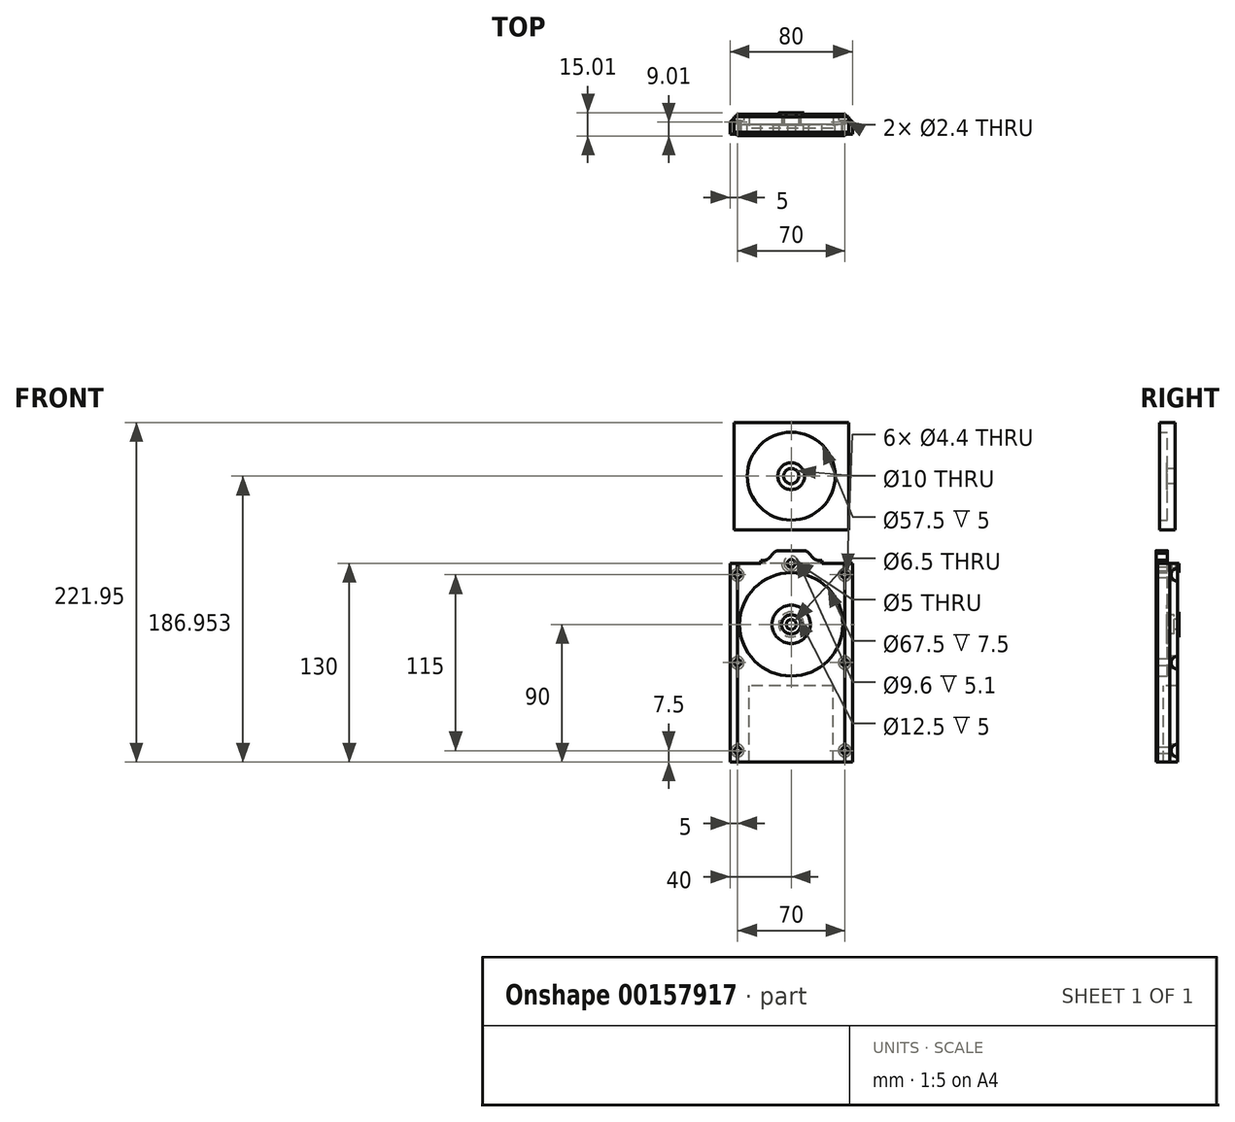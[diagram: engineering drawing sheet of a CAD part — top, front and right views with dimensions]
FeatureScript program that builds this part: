
annotation { "Feature Type Name" : "Feature", "Feature Type Description" : "" }
export const myFeature = defineFeature(function(context is Context, id is Id, definition is map)
    precondition{}
    {
        {
            var Q0;
            Q0=qCreatedBy(makeId("Front.planeOp"),FACE);
            var sketch = newSketch(context, id + "F0", { "sketchPlane" : qUnion([Q0])});
            skLineSegment(sketch, "E0.0", {"start": v(40, -23.23) * mm, "end": v(40, 0.77) * mm});
            skLineSegment(sketch, "E1.0", {"start": v(-40, -23.23) * mm, "end": v(-40, 0.77) * mm});
            skLineSegment(sketch, "E2.bottom", {"start": v(40, 40) * mm, "end": v(19.39, 40) * mm});
            skLineSegment(sketch, "E2.top", {"start": v(40, -40) * mm, "end": v(-40, -40) * mm});
            skLineSegment(sketch, "E2.left", {"start": v(40, 40) * mm, "end": v(40, -40) * mm});
            skLineSegment(sketch, "E2.right", {"start": v(-40, 40) * mm, "end": v(-40, -40) * mm});
            skCircle(sketch, "E3.0", {"center": v(0, 0) * mm, "radius": 3.25 * mm});
            skLineSegment(sketch, "E4.0", {"start": v(7.32, 48.27) * mm, "end": v(-8.54, 48.27) * mm});
            skArc(sketch, "E5.0", {"start": v(-8.54, 48.27) * mm, "mid": v(-10.45, 47.89) * mm, "end": v(-12.08, 46.8) * mm});
            skLineSegment(sketch, "E6.0", {"start": v(-12.08, 46.8) * mm, "end": v(-15.65, 43.23) * mm});
            skArc(sketch, "E7.0", {"start": v(-19.18, 41.77) * mm, "mid": v(-17.27, 42.15) * mm, "end": v(-15.65, 43.23) * mm});
            skLineSegment(sketch, "E8.0", {"start": v(-20.61, 41.77) * mm, "end": v(-19.18, 41.77) * mm});
            skLineSegment(sketch, "E9.0", {"start": v(-20.61, 40) * mm, "end": v(-20.61, 41.77) * mm});
            skArc(sketch, "E10.0", {"start": v(7.32, 48.27) * mm, "mid": v(9.23, 47.89) * mm, "end": v(10.85, 46.8) * mm});
            skLineSegment(sketch, "E11.0", {"start": v(10.85, 46.8) * mm, "end": v(14.42, 43.23) * mm});
            skArc(sketch, "E12.0", {"start": v(17.96, 41.77) * mm, "mid": v(16.05, 42.15) * mm, "end": v(14.42, 43.23) * mm});
            skLineSegment(sketch, "E13.0", {"start": v(19.39, 40) * mm, "end": v(19.39, 41.77) * mm});
            skLineSegment(sketch, "E14", {"start": v(17.96, 41.77) * mm, "end": v(19.39, 41.77) * mm});
            skLineSegment(sketch, "E15.trimOffspring", {"start": v(-20.61, 40) * mm, "end": v(-40, 40) * mm});
            skLineSegment(sketch, "E16", {"start": v(-20.61, 40) * mm, "end": v(19.39, 40) * mm});
            skSolve(sketch);
        }
        {
            var Q0;
            {var subQ4=sQuery(id+"F0.wireOp",EDGE,"E2.bottom");Q0=makeQuery(id+"F0.imprint","IMPRINT",FACE,{"disambiguationData":[TD([[makeQuery(id+"F0.imprint","IMPRINT",EDGE,{"derivedFrom":subQ4}),1.0]])]});}
            extrude(context, id + "F1", {"entities" : qUnion([Q0]), "oppositeDirection" : true, "depth" : 6.5 * mm});
        }
        {
            var Q0;
            Q0=qCreatedBy(makeId("Front.planeOp"),FACE);
            var sketch = newSketch(context, id + "F2", { "sketchPlane" : qUnion([Q0])});
            skCircle(sketch, "E17.0", {"center": v(0, 0) * mm, "radius": 6.3 * mm});
            skLineSegment(sketch, "E18", {"start": v(-40, -40) * mm, "end": v(40, -40) * mm});
            skCircle(sketch, "E19", {"center": v(0, 0) * mm, "radius": 33.75 * mm});
            skLineSegment(sketch, "E20", {"start": v(40, -40) * mm, "end": v(40, 40) * mm});
            skLineSegment(sketch, "E21.0", {"start": v(7.93, 48.27) * mm, "end": v(-7.93, 48.27) * mm});
            skLineSegment(sketch, "E22.0", {"start": v(11.66, 46.56) * mm, "end": v(14.5, 43.42) * mm});
            skLineSegment(sketch, "E23", {"start": v(-40, 40) * mm, "end": v(-40, -40) * mm});
            skLineSegment(sketch, "E24", {"start": v(-20, 40) * mm, "end": v(-40, 40) * mm});
            skLineSegment(sketch, "E25", {"start": v(19.2, 40) * mm, "end": v(40, 40) * mm});
            skLineSegment(sketch, "E26", {"start": v(20, 41.79) * mm, "end": v(20, 40) * mm});
            skLineSegment(sketch, "E27", {"start": v(20, 41.79) * mm, "end": v(18.2, 41.79) * mm});
            skArc(sketch, "E28", {"start": v(14.5, 43.42) * mm, "mid": v(16.18, 42.22) * mm, "end": v(18.2, 41.79) * mm});
            skArc(sketch, "E29", {"start": v(11.66, 46.56) * mm, "mid": v(10, 47.86) * mm, "end": v(7.93, 48.27) * mm});
            skArc(sketch, "E30.MirrorCS", {"start": v(-14.5, 43.42) * mm, "mid": v(-16.18, 42.22) * mm, "end": v(-18.2, 41.79) * mm});
            skLineSegment(sketch, "E31.MirrorCS", {"start": v(-20, 41.79) * mm, "end": v(-20, 40) * mm});
            skLineSegment(sketch, "E32.MirrorCS", {"start": v(-20, 41.79) * mm, "end": v(-18.2, 41.79) * mm});
            skLineSegment(sketch, "E33.MirrorCS", {"start": v(-11.66, 46.56) * mm, "end": v(-14.5, 43.42) * mm});
            skArc(sketch, "E34.MirrorCS", {"start": v(-11.66, 46.56) * mm, "mid": v(-10, 47.86) * mm, "end": v(-7.93, 48.27) * mm});
            skSolve(sketch);
        }
        {
            var Q0;
            Q0 = qSketchRegion(id + "F2", true);
            extrude(context, id + "F3", {"entities" : qUnion([Q0]), "operationType" : NewBodyOperationType.ADD, "depth" : 7.5 * mm});
        }
        {
            var Q0;
            {var subQ0=sQuery(id+"F0.wireOp",EDGE,"E3.0");Q0=makeQuery(id+"F3.boolean.opBoolean","SPLIT",FACE,{"disambiguationData":[TD([makeQuery(id+"F1.opExtrude","SWEPT_FACE",FACE,{"disambiguationData":[OSD([subQ0])]})])],"derivedFrom":makeQuery(id+"F1.opExtrude","CAP_FACE",FACE,{"disambiguationData":[OSD([sQuery(id+"F0.wireOp",EDGE,"E2.bottom"),sQuery(id+"F0.wireOp",EDGE,"E2.top"),sQuery(id+"F0.wireOp",EDGE,"E2.left"),sQuery(id+"F0.wireOp",EDGE,"E2.right"),subQ0,sQuery(id+"F0.wireOp",EDGE,"E15.trimOffspring"),sQuery(id+"F0.wireOp",EDGE,"E16")])],"isStart":true})});}
            var sketch = newSketch(context, id + "F4", { "sketchPlane" : qUnion([Q0])});
            skCircle(sketch, "E35.0", {"center": v(0, 0) * mm, "radius": 3.25 * mm});
            skCircle(sketch, "E36.0", {"center": v(0, 0) * mm, "radius": 12.5 * mm});
            skSolve(sketch);
        }
        {
            var Q0;
            Q0=makeQuery(id+"F4.imprint","IMPRINT",FACE,{"disambiguationData":[TD([[makeQuery(id+"F4.imprint","IMPRINT",EDGE,{"derivedFrom":sQuery(id+"F4.wireOp",EDGE,"E35.0")}),-1.0]])]});
            var Q1;
            Q1 = qConstructionFilter(qBodyType(qCreatedBy(id + "F4" ,EDGE), BodyType.WIRE), ConstructionObject.NO);
            extrude(context, id + "F5", {"entities" : qUnion([Q0]), "operationType" : NewBodyOperationType.ADD, "surfaceEntities" : qUnion([Q1]), "depth" : 0.5 * mm});
        }
        {
            var Q0;
            Q0=makeQuery(id+"F1.opExtrude","CAP_FACE",FACE,{"disambiguationData":[OSD([sQuery(id+"F0.wireOp",EDGE,"E2.bottom"),sQuery(id+"F0.wireOp",EDGE,"E2.top"),sQuery(id+"F0.wireOp",EDGE,"E2.left"),sQuery(id+"F0.wireOp",EDGE,"E2.right"),sQuery(id+"F0.wireOp",EDGE,"E3.0"),sQuery(id+"F0.wireOp",EDGE,"E15.trimOffspring"),sQuery(id+"F0.wireOp",EDGE,"E16")])],"isStart":false});
            var sketch = newSketch(context, id + "F6", { "sketchPlane" : qUnion([Q0])});
            skCircle(sketch, "E37.0", {"center": v(0, 0) * mm, "radius": 3.25 * mm});
            skCircle(sketch, "E38.0", {"center": v(0, 0) * mm, "radius": 8.25 * mm});
            skSolve(sketch);
        }
        {
            var Q0;
            Q0=makeQuery(id+"F6.imprint","IMPRINT",FACE,{"disambiguationData":[TD([[makeQuery(id+"F6.imprint","IMPRINT",EDGE,{"derivedFrom":sQuery(id+"F6.wireOp",EDGE,"E37.0")}),1.0]])]});
            var Q1;
            Q1 = qConstructionFilter(qBodyType(qCreatedBy(id + "F6" ,EDGE), BodyType.WIRE), ConstructionObject.NO);
            extrude(context, id + "F7", {"entities" : qUnion([Q0]), "operationType" : NewBodyOperationType.ADD, "surfaceEntities" : qUnion([Q1]), "depth" : 1 * mm});
        }
        {
            var Q0;
            Q0=makeQuery(id+"F3.opExtrude","SWEPT_FACE",FACE,{"disambiguationData":[OSD([sQuery(id+"F2.wireOp",EDGE,"E18")])]});
            var sketch = newSketch(context, id + "F8", { "sketchPlane" : qUnion([Q0])});
            skLineSegment(sketch, "E39.0", {"start": v(40, -6.5) * mm, "end": v(27.5, -6.5) * mm});
            skLineSegment(sketch, "E40.0", {"start": v(-35, 7.5) * mm, "end": v(35, 7.5) * mm});
            skLineSegment(sketch, "E41", {"start": v(-40, -6.5) * mm, "end": v(-40, 6.5) * mm});
            skPoint(sketch, "E42.orphan", {"position": v(-17.5, 7.5) * mm});
            skLineSegment(sketch, "E43", {"start": v(-35, 6.5) * mm, "end": v(-35, 7.5) * mm});
            skLineSegment(sketch, "E44", {"start": v(-35, 6.5) * mm, "end": v(-40, 6.5) * mm});
            skPoint(sketch, "E45.orphan", {"position": v(-40, 7.5) * mm});
            skLineSegment(sketch, "E46", {"start": v(40, 6.5) * mm, "end": v(35, 6.5) * mm});
            skLineSegment(sketch, "E47", {"start": v(35, 6.5) * mm, "end": v(35, 7.5) * mm});
            skLineSegment(sketch, "E48", {"start": v(27.5, -6.5) * mm, "end": v(27.5, 2.5) * mm});
            skLineSegment(sketch, "E49.MirrorCS", {"start": v(-27.5, -6.5) * mm, "end": v(-27.5, 2.5) * mm});
            skPoint(sketch, "E50.start.orphan", {"position": v(16.14, 2.5) * mm});
            skLineSegment(sketch, "E51.trimOffspring", {"start": v(-27.5, -6.5) * mm, "end": v(-40, -6.5) * mm});
            skLineSegment(sketch, "E52", {"start": v(27.5, 2.5) * mm, "end": v(-27.5, 2.5) * mm});
            skSolve(sketch);
        }
        {
            var Q0;
            {var subQ0=sQuery(id+"F8.wireOp",EDGE,"Noq1iZsC-02XE-U1bK-aTjG-XJcRZ1OyOBWc");var subQ1=sQuery(id+"F8.wireOp",EDGE,"E39.0");var subQ2=makeQuery(id+"F8.imprint","INTERSECT",VERTEX,{"derivedFrom":[subQ1,subQ0]});Q0=makeQuery(id+"F8.imprint","IMPRINT",FACE,{"disambiguationData":[TD([[makeQuery(id+"F8.imprint","IMPRINT",EDGE,{"disambiguationData":[TD([[subQ2,-1.0]])],"derivedFrom":subQ1}),-1.0]])]});}
            var Q1;
            {var subQ7=sQuery(id+"F8.wireOp",EDGE,"E41");Q1=makeQuery(id+"F8.imprint","IMPRINT",FACE,{"disambiguationData":[TD([[makeQuery(id+"F8.imprint","IMPRINT",EDGE,{"derivedFrom":subQ7}),-1.0]])]});}
            var Q2;
            Q2=makeQuery(id+"F8.imprint","IMPRINT",FACE,{"disambiguationData":[TD([[makeQuery(id+"F8.imprint","IMPRINT",EDGE,{"derivedFrom":sQuery(id+"F8.wireOp",EDGE,"E40.0")}),-1.0]])]});
            extrude(context, id + "F9", {"entities" : qUnion([Q0, Q1, Q2]), "operationType" : NewBodyOperationType.ADD, "depth" : 50 * mm});
        }
        {
            var Q0;
            {var subQ0=sQuery(id+"F2.wireOp",EDGE,"F8tKHy5X-4OjT-vRDI-xvfP-sps80f9JvOj5");var subQ1=sQuery(id+"F2.wireOp",EDGE,"E18");var subQ2=makeQuery(id+"F3.opExtrude","SWEPT_FACE",FACE,{"disambiguationData":[OSD([subQ1])]});Q0=makeQuery(id+"F9.boolean.opBoolean","SPLIT",FACE,{"disambiguationData":[TD([makeQuery(id+"F3.opExtrude","CAP_FACE",FACE,{"disambiguationData":[OSD([sQuery(id+"F2.wireOp",EDGE,"43ff70fc-8323-4c3b-be4f-e7dcd28128a2.0"),sQuery(id+"F2.wireOp",EDGE,"6a53bcd3-b350-4012-b1e6-f17d590e4d40.0"),sQuery(id+"F2.wireOp",EDGE,"d2d7cf8e-e79f-49f9-bd9e-9d3b9ff60ceb.0"),sQuery(id+"F2.wireOp",EDGE,"d467ac46-905b-445b-963e-ac5b84aad985.0"),sQuery(id+"F2.wireOp",EDGE,"bd112014-28de-4375-aa5b-1523fa892efe.0"),sQuery(id+"F2.wireOp",EDGE,"0f5d5f43-bfa9-40f1-814d-f970481e9f5a.0"),sQuery(id+"F2.wireOp",EDGE,"7188da67-afae-4a6f-96a4-23c76f9ca605.0"),sQuery(id+"F2.wireOp",EDGE,"be224130-12d7-4de9-89d5-a9a642df7f72.0"),sQuery(id+"F2.wireOp",EDGE,"49c1cc58-9d2c-462a-8fa2-00916c70b713.0"),sQuery(id+"F2.wireOp",EDGE,"3bd6d884-65c0-4bce-9f69-8ca00f18da7b.0"),sQuery(id+"F2.wireOp",EDGE,"5123f48f-925f-46dd-863a-fc0157268591"),sQuery(id+"F2.wireOp",EDGE,"62nOXX7M-Kpb4-EMSY-4AHT-RUUfIk4w2igv"),subQ1,subQ0,sQuery(id+"F2.wireOp",EDGE,"Frdd6jCd-H3OT-73R4-LAr2-6LJI8BfQxRTi"),sQuery(id+"F2.wireOp",EDGE,"cVu9BNWQ-aUoj-CZYY-OFb3-C1fxlzU4T7I8"),sQuery(id+"F2.wireOp",EDGE,"E19")])],"isStart":false}),subQ2,makeQuery(id+"F3.opExtrude","SWEPT_FACE",FACE,{"disambiguationData":[OSD([subQ0])]}),makeQuery(id+"F9.opExtrude","SWEPT_FACE",FACE,{"disambiguationData":[OSD([sQuery(id+"F8.wireOp",EDGE,"E40.0")])]}),makeQuery(id+"F9.opExtrude","SWEPT_FACE",FACE,{"disambiguationData":[OSD([sQuery(id+"F8.wireOp",EDGE,"Noq1iZsC-02XE-U1bK-aTjG-XJcRZ1OyOBWc")])]}),makeQuery(id+"F9.opExtrude","SWEPT_FACE",FACE,{"disambiguationData":[OSD([sQuery(id+"F8.wireOp",EDGE,"E46")])]}),makeQuery(id+"F9.opExtrude","SWEPT_FACE",FACE,{"disambiguationData":[OSD([sQuery(id+"F8.wireOp",EDGE,"E47")])]})])],"derivedFrom":subQ2});}
            var Q1;
            {var subQ0=sQuery(id+"F8.wireOp",EDGE,"E40.0");var subQ1=sQuery(id+"F8.wireOp",EDGE,"E44");var subQ2=sQuery(id+"F8.wireOp",EDGE,"E43");var subQ3=sQuery(id+"F2.wireOp",EDGE,"62nOXX7M-Kpb4-EMSY-4AHT-RUUfIk4w2igv");var subQ4=sQuery(id+"F2.wireOp",EDGE,"E18");Q1=makeQuery(id+"F9.boolean.opBoolean","SPLIT",FACE,{"disambiguationData":[TD([makeQuery(id+"F3.opExtrude","CAP_FACE",FACE,{"disambiguationData":[OSD([sQuery(id+"F2.wireOp",EDGE,"43ff70fc-8323-4c3b-be4f-e7dcd28128a2.0"),sQuery(id+"F2.wireOp",EDGE,"6a53bcd3-b350-4012-b1e6-f17d590e4d40.0"),sQuery(id+"F2.wireOp",EDGE,"d2d7cf8e-e79f-49f9-bd9e-9d3b9ff60ceb.0"),sQuery(id+"F2.wireOp",EDGE,"d467ac46-905b-445b-963e-ac5b84aad985.0"),sQuery(id+"F2.wireOp",EDGE,"bd112014-28de-4375-aa5b-1523fa892efe.0"),sQuery(id+"F2.wireOp",EDGE,"0f5d5f43-bfa9-40f1-814d-f970481e9f5a.0"),sQuery(id+"F2.wireOp",EDGE,"7188da67-afae-4a6f-96a4-23c76f9ca605.0"),sQuery(id+"F2.wireOp",EDGE,"be224130-12d7-4de9-89d5-a9a642df7f72.0"),sQuery(id+"F2.wireOp",EDGE,"49c1cc58-9d2c-462a-8fa2-00916c70b713.0"),sQuery(id+"F2.wireOp",EDGE,"3bd6d884-65c0-4bce-9f69-8ca00f18da7b.0"),sQuery(id+"F2.wireOp",EDGE,"5123f48f-925f-46dd-863a-fc0157268591"),subQ3,subQ4,sQuery(id+"F2.wireOp",EDGE,"F8tKHy5X-4OjT-vRDI-xvfP-sps80f9JvOj5"),sQuery(id+"F2.wireOp",EDGE,"Frdd6jCd-H3OT-73R4-LAr2-6LJI8BfQxRTi"),sQuery(id+"F2.wireOp",EDGE,"cVu9BNWQ-aUoj-CZYY-OFb3-C1fxlzU4T7I8"),sQuery(id+"F2.wireOp",EDGE,"E19")])],"isStart":false}),makeQuery(id+"F3.opExtrude","SWEPT_FACE",FACE,{"disambiguationData":[OSD([subQ3])]}),makeQuery(id+"F9.opExtrude","CAP_FACE",FACE,{"disambiguationData":[OSD([sQuery(id+"F8.wireOp",EDGE,"E39.0"),subQ0,sQuery(id+"F8.wireOp",EDGE,"E41"),sQuery(id+"F8.wireOp",EDGE,"Noq1iZsC-02XE-U1bK-aTjG-XJcRZ1OyOBWc"),sQuery(id+"F8.wireOp",EDGE,"2a7uyrXM-BAuq-J7Q7-3D6L-PmTSweeUyeWE"),sQuery(id+"F8.wireOp",EDGE,"a981deb7-1a47-4182-8a64-5c5e49a7536c0.MirrorCS"),sQuery(id+"F8.wireOp",EDGE,"E50"),subQ2,subQ1,sQuery(id+"F8.wireOp",EDGE,"E46"),sQuery(id+"F8.wireOp",EDGE,"E47")])],"isStart":true}),makeQuery(id+"F9.opExtrude","SWEPT_FACE",FACE,{"disambiguationData":[OSD([subQ0])]}),makeQuery(id+"F9.opExtrude","SWEPT_FACE",FACE,{"disambiguationData":[OSD([subQ2])]}),makeQuery(id+"F9.opExtrude","SWEPT_FACE",FACE,{"disambiguationData":[OSD([subQ1])]})])],"derivedFrom":makeQuery(id+"F3.opExtrude","SWEPT_FACE",FACE,{"disambiguationData":[OSD([subQ4])]})});}
            extrude(context, id + "F10", {"entities" : qUnion([Q0, Q1]), "operationType" : NewBodyOperationType.REMOVE, "oppositeDirection" : true, "depth" : 120 * mm});
        }
        {
            var Q0;
            {var subQ0=sQuery(id+"F8.wireOp",EDGE,"E39.0");Q0=makeQuery(id+"F9.boolean.opBoolean","MERGE",FACE,{"derivedFrom":[makeQuery(id+"F1.opExtrude","CAP_FACE",FACE,{"disambiguationData":[OSD([sQuery(id+"F0.wireOp",EDGE,"E2.bottom"),sQuery(id+"F0.wireOp",EDGE,"E2.top"),sQuery(id+"F0.wireOp",EDGE,"E2.left"),sQuery(id+"F0.wireOp",EDGE,"E2.right"),sQuery(id+"F0.wireOp",EDGE,"E3.0"),sQuery(id+"F0.wireOp",EDGE,"E15.trimOffspring"),sQuery(id+"F0.wireOp",EDGE,"E16")])],"isStart":false}),makeQuery(id+"F9.opExtrude","SWEPT_FACE",FACE,{"disambiguationData":[OSD([subQ0]),TDD([makeQuery(id+"F8.imprint","IMPRINT",EDGE,{"disambiguationData":[TD([[makeQuery(id+"F8.imprint","INTERSECT",VERTEX,{"derivedFrom":[subQ0,sQuery(id+"F8.wireOp",EDGE,"Noq1iZsC-02XE-U1bK-aTjG-XJcRZ1OyOBWc")]}),-1.0]])],"derivedFrom":subQ0})])]}),makeQuery(id+"F9.opExtrude","SWEPT_FACE",FACE,{"disambiguationData":[OSD([subQ0]),TDD([makeQuery(id+"F8.imprint","IMPRINT",EDGE,{"disambiguationData":[TD([[makeQuery(id+"F8.imprint","INTERSECT",VERTEX,{"derivedFrom":[subQ0,sQuery(id+"F8.wireOp",EDGE,"E41")]}),1.0]])],"derivedFrom":subQ0})])]})]});}
            var sketch = newSketch(context, id + "F11", { "sketchPlane" : qUnion([Q0])});
            skLineSegment(sketch, "E53.0", {"start": v(-35, 40) * mm, "end": v(35, 40) * mm});
            skCircle(sketch, "E54", {"center": v(35, 32.5) * mm, "radius": 3.48 * mm});
            skCircle(sketch, "E55", {"center": v(35, -25) * mm, "radius": 3.24 * mm});
            skCircle(sketch, "E56.MirrorC", {"center": v(35, -82.5) * mm, "radius": 3.48 * mm});
            skCircle(sketch, "E57.MirrorC", {"center": v(-35, 32.5) * mm, "radius": 3.48 * mm});
            skCircle(sketch, "E58.MirrorC", {"center": v(-35, -25) * mm, "radius": 3.24 * mm});
            skCircle(sketch, "E59.MirrorC", {"center": v(-35, -82.5) * mm, "radius": 3.48 * mm});
            skLineSegment(sketch, "E60", {"start": v(35, -25) * mm, "end": v(-35, -25) * mm});
            skSolve(sketch);
        }
        {
            var Q0;
            Q0=sQuery(id+"F11.wireOp",VERTEX,"E54.center");
            var Q1;
            Q1=sQuery(id+"F11.wireOp",VERTEX,"E55.center");
            var Q2;
            Q2=sQuery(id+"F11.wireOp",VERTEX,"E56.MirrorC.center");
            var Q3;
            Q3=sQuery(id+"F11.wireOp",VERTEX,"E59.MirrorC.center");
            var Q4;
            Q4=sQuery(id+"F11.wireOp",VERTEX,"E58.MirrorC.center");
            var Q5;
            Q5=sQuery(id+"F11.wireOp",VERTEX,"E57.MirrorC.center");
            var Q6;
            Q6=makeQuery(id+"F1.opExtrude","SWEPT_BODY",BODY,{"disambiguationData":[OSD([sQuery(id+"F0.wireOp",EDGE,"E2.bottom"),sQuery(id+"F0.wireOp",EDGE,"E2.top"),sQuery(id+"F0.wireOp",EDGE,"E2.left"),sQuery(id+"F0.wireOp",EDGE,"E2.right"),sQuery(id+"F0.wireOp",EDGE,"E3.0"),sQuery(id+"F0.wireOp",EDGE,"E15.trimOffspring"),sQuery(id+"F0.wireOp",EDGE,"E16")])]});
            hole(context, id + "F12", {"style" : HoleStyle.C_BORE, "endStyle" : HoleEndStyle.THROUGH, "standardTappedOrClearance" : lookupTablePath({ "standard" : "ISO", "fit" : "Normal", "size" : "M4", "type" : "Clearance" }), "standardBlindInLast" : lookupTablePath({ "fit" : "Standard", "standard" : "ISO", "size" : "M4", "type" : "Clearance" }), "holeDiameter" : 4.4 * mm, "cBoreDiameter" : 8.25 * mm, "cBoreDepth" : 4 * mm, "locations" : qUnion([Q0, Q1, Q2, Q3, Q4, Q5]), "scope" : qUnion([Q6]), "isTappedThrough" : true, "startStyle" : HoleStartStyle.SKETCH});
        }
        {
            var Q0;
            {var subQ0=sQuery(id+"F0.wireOp",EDGE,"E2.left");Q0=makeQuery(id+"F9.boolean.opBoolean","MERGE",EDGE,{"derivedFrom":[makeQuery(id+"F1.opExtrude","CAP_EDGE",EDGE,{"disambiguationData":[OSD([subQ0])],"isStart":false}),makeQuery(id+"F9.opExtrude","SWEPT_EDGE",EDGE,{"disambiguationData":[OSD([sQuery(id+"F0.wireOp",EDGE,"E2.top"),subQ0,sQuery(id+"F2.wireOp",EDGE,"E18"),sQuery(id+"F2.wireOp",EDGE,"E20"),sQuery(id+"F8.wireOp",EDGE,"E39.0")])]})]});}
            var Q1;
            Q1=makeQuery(id+"F9.boolean.opBoolean","MERGE",EDGE,{"derivedFrom":[makeQuery(id+"F1.opExtrude","CAP_EDGE",EDGE,{"disambiguationData":[OSD([sQuery(id+"F0.wireOp",EDGE,"E2.right")])],"isStart":false}),makeQuery(id+"F9.opExtrude","SWEPT_EDGE",EDGE,{"disambiguationData":[OSD([sQuery(id+"F8.wireOp",EDGE,"E41"),sQuery(id+"F8.wireOp",EDGE,"E51.trimOffspring")])]})]});
            chamfer(context, id + "F13", {"entities" : qUnion([Q0, Q1]), "width" : 5 * mm, "tangentPropagation" : true});
        }
        {
            var Q0;
            Q0=makeQuery(id+"F9.boolean.opBoolean","MERGE",FACE,{"derivedFrom":[makeQuery(id+"F3.opExtrude","CAP_FACE",FACE,{"disambiguationData":[OSD([sQuery(id+"F2.wireOp",EDGE,"E18"),sQuery(id+"F2.wireOp",EDGE,"E19"),sQuery(id+"F2.wireOp",EDGE,"E20"),sQuery(id+"F2.wireOp",EDGE,"E21.0"),sQuery(id+"F2.wireOp",EDGE,"3787cd86-f1fa-4794-8e68-ac3dcc2af5fc.0"),sQuery(id+"F2.wireOp",EDGE,"74d55069-eddd-4e39-9dde-a36961150f2b.0"),sQuery(id+"F2.wireOp",EDGE,"E22.0"),sQuery(id+"F2.wireOp",EDGE,"11a16c4b-345a-4e4a-a94e-f19d0f1f867e.0"),sQuery(id+"F2.wireOp",EDGE,"947ffe7e-d47e-463b-96ee-cae2d2102a52.0"),sQuery(id+"F2.wireOp",EDGE,"126ff08f-ab56-4892-8ac0-91e981eb14b4.0"),sQuery(id+"F2.wireOp",EDGE,"3d538390-cc80-4456-be9c-b5f9d3f663fc.0"),sQuery(id+"F2.wireOp",EDGE,"f2edf121-58e0-41d3-ac7d-7312daae6a6d.0"),sQuery(id+"F2.wireOp",EDGE,"jHMJFMlt-CE4D-w7tA-MRXQ-V35x0nQWXnLe"),sQuery(id+"F2.wireOp",EDGE,"8Z37ihXP-Yr2x-WDWQ-3fvC-AVeg1EhtUArQ"),sQuery(id+"F2.wireOp",EDGE,"E23"),sQuery(id+"F2.wireOp",EDGE,"E24"),sQuery(id+"F2.wireOp",EDGE,"E25")])],"isStart":false}),makeQuery(id+"F9.opExtrude","SWEPT_FACE",FACE,{"disambiguationData":[OSD([sQuery(id+"F8.wireOp",EDGE,"E40.0")])]})]});
            var sketch = newSketch(context, id + "F14", { "sketchPlane" : qUnion([Q0])});
            skCircle(sketch, "E61", {"center": v(0, 40) * mm, "radius": 2.5 * mm});
            skSolve(sketch);
        }
        {
            var Q0;
            Q0 = qSketchRegion(id + "F14", true);
            extrude(context, id + "F15", {"entities" : qUnion([Q0]), "operationType" : NewBodyOperationType.REMOVE, "endBound" : BoundingType.THROUGH_ALL, "oppositeDirection" : true, "depth" : 25 * mm});
        }
        {
            var Q0;
            Q0=qCreatedBy(makeId("Front.planeOp"),FACE);
            var sketch = newSketch(context, id + "F16", { "sketchPlane" : qUnion([Q0])});
            skCircle(sketch, "E62", {"center": v(0, 40) * mm, "radius": 4.8 * mm});
            skSolve(sketch);
        }
        {
            var Q0;
            Q0 = qSketchRegion(id + "F16", true);
            extrude(context, id + "F17", {"entities" : qUnion([Q0]), "operationType" : NewBodyOperationType.REMOVE, "oppositeDirection" : true, "depth" : 5 * mm});
        }
        {
            var Q0;
            Q0=makeQuery(id+"F9.boolean.opBoolean","MERGE",FACE,{"derivedFrom":[makeQuery(id+"F1.opExtrude","CAP_FACE",FACE,{"disambiguationData":[OSD([sQuery(id+"F0.wireOp",EDGE,"E2.bottom"),sQuery(id+"F0.wireOp",EDGE,"E2.top"),sQuery(id+"F0.wireOp",EDGE,"E2.left"),sQuery(id+"F0.wireOp",EDGE,"E2.right"),sQuery(id+"F0.wireOp",EDGE,"E3.0"),sQuery(id+"F0.wireOp",EDGE,"E15.trimOffspring"),sQuery(id+"F0.wireOp",EDGE,"E16")])],"isStart":false}),makeQuery(id+"F9.opExtrude","SWEPT_FACE",FACE,{"disambiguationData":[OSD([sQuery(id+"F8.wireOp",EDGE,"E39.0")])]}),makeQuery(id+"F9.opExtrude","SWEPT_FACE",FACE,{"disambiguationData":[OSD([sQuery(id+"F8.wireOp",EDGE,"E51.trimOffspring")])]})]});
            var sketch = newSketch(context, id + "F18", { "sketchPlane" : qUnion([Q0])});
            skCircle(sketch, "E63", {"center": v(0, 40) * mm, "radius": 3.3 * mm});
            skSolve(sketch);
        }
        {
            var Q0;
            Q0 = qSketchRegion(id + "F18", true);
            extrude(context, id + "F19", {"entities" : qUnion([Q0]), "operationType" : NewBodyOperationType.REMOVE, "oppositeDirection" : true, "depth" : 2.5 * mm});
        }
        {
            var Q0;
            Q0=makeQuery(id+"F17.boolean.opBoolean","MERGE",FACE,{"derivedFrom":[makeQuery(id+"F3.opExtrude","CAP_FACE",FACE,{"disambiguationData":[OSD([sQuery(id+"F2.wireOp",EDGE,"E18"),sQuery(id+"F2.wireOp",EDGE,"E19"),sQuery(id+"F2.wireOp",EDGE,"E20"),sQuery(id+"F2.wireOp",EDGE,"E21.0"),sQuery(id+"F2.wireOp",EDGE,"3787cd86-f1fa-4794-8e68-ac3dcc2af5fc.0"),sQuery(id+"F2.wireOp",EDGE,"74d55069-eddd-4e39-9dde-a36961150f2b.0"),sQuery(id+"F2.wireOp",EDGE,"E22.0"),sQuery(id+"F2.wireOp",EDGE,"11a16c4b-345a-4e4a-a94e-f19d0f1f867e.0"),sQuery(id+"F2.wireOp",EDGE,"947ffe7e-d47e-463b-96ee-cae2d2102a52.0"),sQuery(id+"F2.wireOp",EDGE,"126ff08f-ab56-4892-8ac0-91e981eb14b4.0"),sQuery(id+"F2.wireOp",EDGE,"3d538390-cc80-4456-be9c-b5f9d3f663fc.0"),sQuery(id+"F2.wireOp",EDGE,"f2edf121-58e0-41d3-ac7d-7312daae6a6d.0"),sQuery(id+"F2.wireOp",EDGE,"jHMJFMlt-CE4D-w7tA-MRXQ-V35x0nQWXnLe"),sQuery(id+"F2.wireOp",EDGE,"8Z37ihXP-Yr2x-WDWQ-3fvC-AVeg1EhtUArQ"),sQuery(id+"F2.wireOp",EDGE,"E23"),sQuery(id+"F2.wireOp",EDGE,"E24"),sQuery(id+"F2.wireOp",EDGE,"E25")])],"isStart":true}),makeQuery(id+"F17.opExtrude","CAP_FACE",FACE,{"disambiguationData":[OSD([sQuery(id+"F16.wireOp",EDGE,"E62")])],"isStart":true})]});
            var sketch = newSketch(context, id + "F20", { "sketchPlane" : qUnion([Q0])});
            skCircle(sketch, "E64.0", {"center": v(0, 40) * mm, "radius": 4.8 * mm});
            skSolve(sketch);
        }
        {
            var Q0;
            Q0 = qSketchRegion(id + "F20", true);
            extrude(context, id + "F21", {"entities" : qUnion([Q0]), "operationType" : NewBodyOperationType.REMOVE, "oppositeDirection" : true, "depth" : 0.1 * mm});
        }
        {
            var Q0;
            Q0=makeQuery(id+"F9.boolean.opBoolean","MERGE",FACE,{"derivedFrom":[makeQuery(id+"F1.opExtrude","CAP_FACE",FACE,{"disambiguationData":[OSD([sQuery(id+"F0.wireOp",EDGE,"E2.bottom"),sQuery(id+"F0.wireOp",EDGE,"E2.top"),sQuery(id+"F0.wireOp",EDGE,"E2.left"),sQuery(id+"F0.wireOp",EDGE,"E2.right"),sQuery(id+"F0.wireOp",EDGE,"E3.0"),sQuery(id+"F0.wireOp",EDGE,"E15.trimOffspring"),sQuery(id+"F0.wireOp",EDGE,"E16")])],"isStart":false}),makeQuery(id+"F9.opExtrude","SWEPT_FACE",FACE,{"disambiguationData":[OSD([sQuery(id+"F8.wireOp",EDGE,"E39.0")])]}),makeQuery(id+"F9.opExtrude","SWEPT_FACE",FACE,{"disambiguationData":[OSD([sQuery(id+"F8.wireOp",EDGE,"E51.trimOffspring")])]})]});
            var sketch = newSketch(context, id + "F22", { "sketchPlane" : qUnion([Q0])});
            skArc(sketch, "E65.0", {"start": v(-3.3, 40) * mm, "mid": v(0, 36.7) * mm, "end": v(3.3, 40) * mm});
            skArc(sketch, "E66", {"start": v(-6.25, 40) * mm, "mid": v(0, 33.75) * mm, "end": v(6.25, 40) * mm});
            skLineSegment(sketch, "E67.0", {"start": v(3.3, 40) * mm, "end": v(6.25, 40) * mm});
            skLineSegment(sketch, "E68.0", {"start": v(-6.25, 40) * mm, "end": v(-3.3, 40) * mm});
            skPoint(sketch, "E69.orphan", {"position": v(35, 40) * mm});
            skPoint(sketch, "E70.orphan", {"position": v(-35, 40) * mm});
            skSolve(sketch);
        }
        {
            var Q0;
            Q0 = qSketchRegion(id + "F22", true);
            extrude(context, id + "F23", {"entities" : qUnion([Q0]), "operationType" : NewBodyOperationType.ADD, "depth" : 1 * mm});
        }
        {
            var Q0;
            Q0=makeQuery(id+"F5.opExtrude","CAP_FACE",FACE,{"disambiguationData":[OSD([sQuery(id+"F4.wireOp",EDGE,"E35.0"),sQuery(id+"F4.wireOp",EDGE,"E36.0")])],"isStart":false});
            var sketch = newSketch(context, id + "F24", { "sketchPlane" : qUnion([Q0])});
            skCircle(sketch, "E71", {"center": v(0, 0) * mm, "radius": 6.25 * mm});
            skSolve(sketch);
        }
        {
            var Q0;
            Q0 = qSketchRegion(id + "F24", true);
            extrude(context, id + "F25", {"entities" : qUnion([Q0]), "operationType" : NewBodyOperationType.REMOVE, "oppositeDirection" : true, "depth" : 5 * mm});
        }
        {
            var Q0;
            {var subQ5=sQuery(id+"F0.wireOp",EDGE,"E16");var subQ6=sQuery(id+"F0.wireOp",EDGE,"E15.trimOffspring");var subQ7=sQuery(id+"F0.wireOp",EDGE,"E2.right");var subQ8=sQuery(id+"F0.wireOp",EDGE,"E2.bottom");var subQ9=sQuery(id+"F2.wireOp",EDGE,"E25");var subQ10=sQuery(id+"F2.wireOp",EDGE,"E24");Q0=makeQuery(id+"F23.boolean.opBoolean","MERGE",FACE,{"derivedFrom":[makeQuery(id+"F15.boolean.opBoolean","SPLIT",FACE,{"disambiguationData":[TD([makeQuery(id+"F1.opExtrude","SWEPT_FACE",FACE,{"disambiguationData":[OSD([subQ7])]})])],"derivedFrom":makeQuery(id+"F3.boolean.opBoolean","MERGE",FACE,{"derivedFrom":[makeQuery(id+"F1.opExtrude","SWEPT_FACE",FACE,{"disambiguationData":[OSD([subQ8,subQ6,subQ5])]}),makeQuery(id+"F3.opExtrude","SWEPT_FACE",FACE,{"disambiguationData":[OSD([subQ10])]}),makeQuery(id+"F3.opExtrude","SWEPT_FACE",FACE,{"disambiguationData":[OSD([subQ9])]})]})}),makeQuery(id+"F23.opExtrude","SWEPT_FACE",FACE,{"disambiguationData":[OSD([sQuery(id+"F22.wireOp",EDGE,"E67.0")])]})]});}
            var sketch = newSketch(context, id + "F26", { "sketchPlane" : qUnion([Q0])});
            skPoint(sketch, "E72", {"position": v(-35, 1.5) * mm});
            skPoint(sketch, "E73.MirrorP", {"position": v(35, 1.5) * mm});
            skSolve(sketch);
        }
        {
            var Q0;
            Q0=sQuery(id+"F26.wireOp",VERTEX,"E72");
            var Q1;
            Q1=sQuery(id+"F26.wireOp",VERTEX,"E73.MirrorP");
            var Q2;
            Q2=makeQuery(id+"F1.opExtrude","SWEPT_BODY",BODY,{"disambiguationData":[OSD([sQuery(id+"F0.wireOp",EDGE,"E2.bottom"),sQuery(id+"F0.wireOp",EDGE,"E2.top"),sQuery(id+"F0.wireOp",EDGE,"E2.left"),sQuery(id+"F0.wireOp",EDGE,"E2.right"),sQuery(id+"F0.wireOp",EDGE,"E3.0"),sQuery(id+"F0.wireOp",EDGE,"E15.trimOffspring"),sQuery(id+"F0.wireOp",EDGE,"E16")])]});
            hole(context, id + "F27", {"style" : HoleStyle.SIMPLE, "endStyle" : HoleEndStyle.BLIND, "standardTappedOrClearance" : lookupTablePath({ "standard" : "ISO", "engagement" : "75%", "pitch" : "0.6 mm", "size" : "M3", "type" : "Tapped" }), "standardBlindInLast" : lookupTablePath({ "standard" : "ISO", "engagement" : "75%", "pitch" : "0.6 mm", "size" : "M3", "type" : "Tapped" }), "holeDiameter" : 2.4 * mm, "holeDepth" : 2.5 * mm, "locations" : qUnion([Q0, Q1]), "scope" : qUnion([Q2]), "startStyle" : HoleStartStyle.SKETCH});
        }
        {
            var Q0;
            Q0=qCreatedBy(makeId("Front.planeOp"),FACE);
            var sketch = newSketch(context, id + "F28", { "sketchPlane" : qUnion([Q0])});
            skLineSegment(sketch, "E74.bottom", {"start": v(-37.5, 131.95) * mm, "end": v(37.5, 131.95) * mm});
            skLineSegment(sketch, "E74.top", {"start": v(-37.5, 61.95) * mm, "end": v(37.5, 61.95) * mm});
            skLineSegment(sketch, "E74.left", {"start": v(-37.5, 131.95) * mm, "end": v(-37.5, 61.95) * mm});
            skLineSegment(sketch, "E74.right", {"start": v(37.5, 131.95) * mm, "end": v(37.5, 61.95) * mm});
            skCircle(sketch, "E75", {"center": v(0, 96.95) * mm, "radius": 5 * mm});
            skPoint(sketch, "E75.centerSnap0", {"position": v(-37.5, 96.95) * mm});
            skSolve(sketch);
        }
        {
            var Q0;
            Q0 = qSketchRegion(id + "F28", true);
            extrude(context, id + "F29", {"entities" : qUnion([Q0]), "oppositeDirection" : true, "depth" : 5 * mm});
        }
        {
            var Q0;
            Q0=makeQuery(id+"F29.opExtrude","CAP_FACE",FACE,{"disambiguationData":[OSD([sQuery(id+"F28.wireOp",EDGE,"E74.bottom"),sQuery(id+"F28.wireOp",EDGE,"E74.top"),sQuery(id+"F28.wireOp",EDGE,"E74.left"),sQuery(id+"F28.wireOp",EDGE,"E74.right")])],"isStart":true});
            var sketch = newSketch(context, id + "F30", { "sketchPlane" : qUnion([Q0])});
            skCircle(sketch, "E76", {"center": v(0, 96.95) * mm, "radius": 28.75 * mm});
            skPoint(sketch, "E76.centerSnap0", {"position": v(-37.5, 96.95) * mm});
            skSolve(sketch);
        }
        {
            var Q0;
            Q0=makeQuery(id+"F30.imprint","IMPRINT",FACE,{"disambiguationData":[TD([[makeQuery(id+"F30.imprint","IMPRINT",EDGE,{"derivedFrom":sQuery(id+"F30.wireOp",EDGE,"E76")}),-1.0]])]});
            extrude(context, id + "F31", {"entities" : qUnion([Q0]), "operationType" : NewBodyOperationType.ADD, "depth" : 5 * mm});
        }
        {
            var Q0;
            Q0=makeQuery(id+"F29.opExtrude","CAP_FACE",FACE,{"disambiguationData":[OSD([sQuery(id+"F28.wireOp",EDGE,"E74.bottom"),sQuery(id+"F28.wireOp",EDGE,"E74.top"),sQuery(id+"F28.wireOp",EDGE,"E74.left"),sQuery(id+"F28.wireOp",EDGE,"E74.right"),sQuery(id+"F28.wireOp",EDGE,"E75")])],"isStart":true});
            var sketch = newSketch(context, id + "F32", { "sketchPlane" : qUnion([Q0])});
            skCircle(sketch, "E77.0", {"center": v(0, 96.95) * mm, "radius": 5 * mm});
            skCircle(sketch, "E78", {"center": v(0, 96.95) * mm, "radius": 8.75 * mm});
            skSolve(sketch);
        }
        {
            var Q0;
            Q0 = qSketchRegion(id + "F32", true);
            extrude(context, id + "F33", {"entities" : qUnion([Q0]), "operationType" : NewBodyOperationType.ADD, "depth" : 0.5 * mm});
        }
    });
